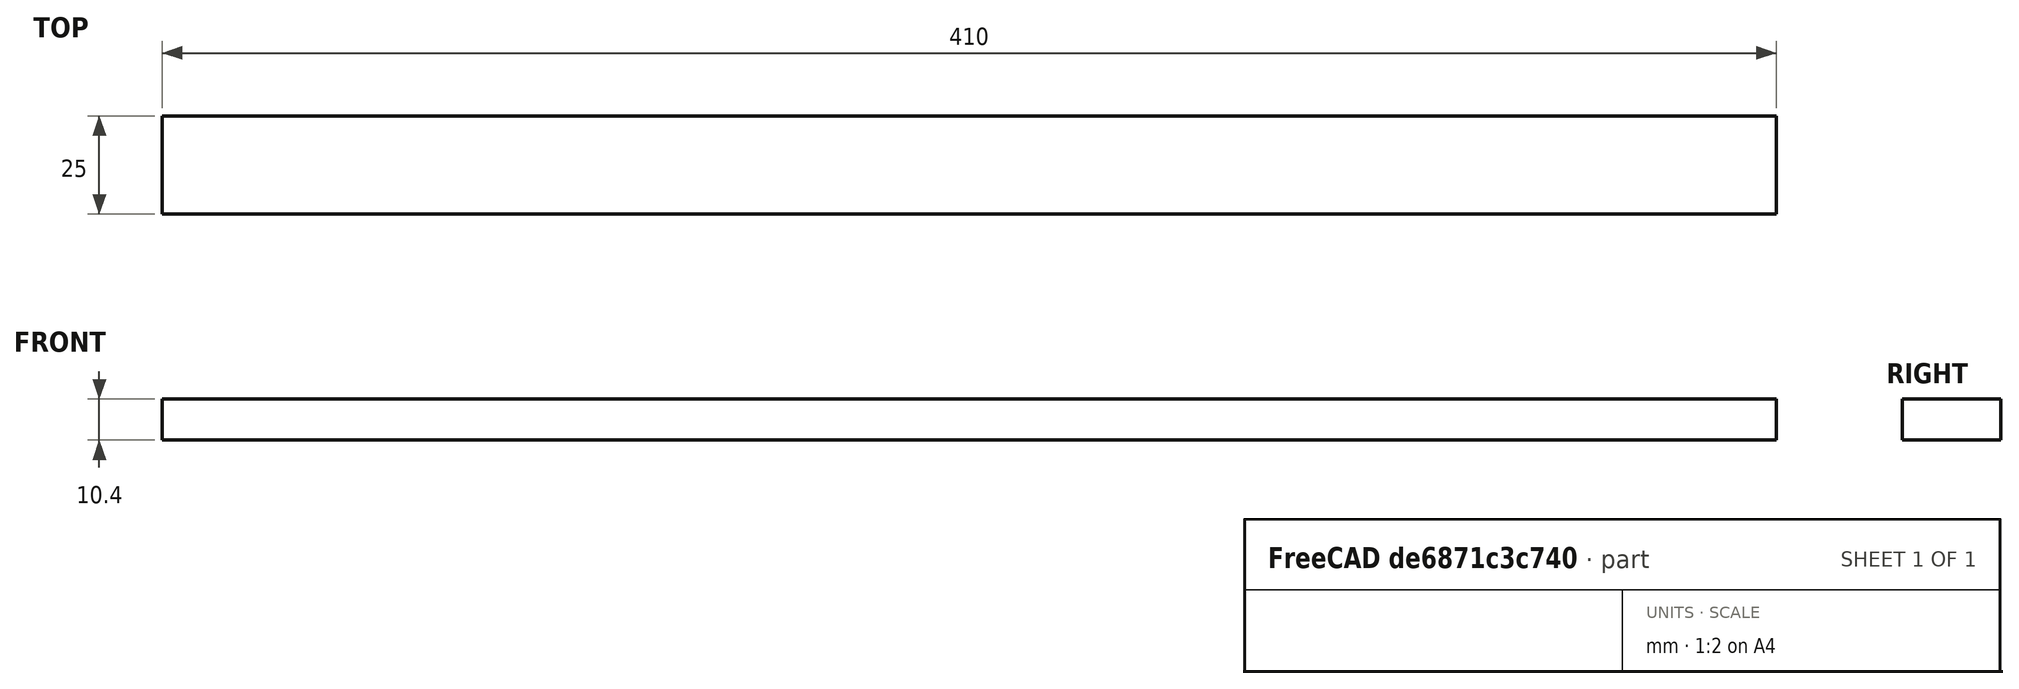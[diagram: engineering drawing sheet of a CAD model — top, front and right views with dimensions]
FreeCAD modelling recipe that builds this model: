
FCSTD DOCUMENT  (FreeCAD 0.19R24267 +99 (Git))
Label: Laufschinen
License: All rights reserved
LicenseURL: http://en.wikipedia.org/wiki/All_rights_reserved
objects: TechDraw::DrawProjGroupItem×3, TechDraw::DrawProjGroup×3, TechDraw::DrawViewDimension×3, Sketcher::SketchObject×1, PartDesign::Pad×1, PartDesign::Body×1, TechDraw::DrawSVGTemplate×1, TechDraw::DrawPage×1
note: 4 computed .brp shape members not serialized (recipe doc carries the construction recipe); baked Part::Feature solids carry a one-line shape summary decoded from their .brp

FEATURE [Sketcher::SketchObject] Sketch
  FullyConstrained = true
  MapMode = 5
  Support = -> [XY_Plane]
  sketch-geometry (4):
    g0: LineSegment StartX=-205 StartY=12.5 StartZ=0 EndX=205 EndY=12.5 EndZ=0
    g1: LineSegment StartX=205 StartY=12.5 StartZ=0 EndX=205 EndY=-12.5 EndZ=0
    g2: LineSegment StartX=205 StartY=-12.5 StartZ=0 EndX=-205 EndY=-12.5 EndZ=0
    g3: LineSegment StartX=-205 StartY=-12.5 StartZ=0 EndX=-205 EndY=12.5 EndZ=0
  constraints (11):
    c: Coincident(g0,g1)
    c: Coincident(g1,g2)
    c: Coincident(g2,g3)
    c: Coincident(g3,g0)
    c: Horizontal(g0)
    c: Horizontal(g2)
    c: Vertical(g1)
    c: Vertical(g3)
    c: DistanceX(g0,g0) = 410
    c: Symmetric(g0,g1,g-1)
    c: DistanceY(g1,g1) = 25
FEATURE [PartDesign::Pad] Pad
  Direction = (1,1,1)
  Length = 10.4
  Length2 = 100
  Profile = -> Sketch
  Type = 0
FEATURE [PartDesign::Body] Body
  Group = -> [Sketch,Pad]
  Origin = -> Origin
  Tip = -> Pad
FEATURE [TechDraw::DrawSVGTemplate] Template
  EditableTexts = APPROVER_NAME=APPROVER NAME; AUTHOR_NAME=AUTHOR NAME; DATE=YYYY-MM-DD; DN=DN; DOCUMENT_TYPE=Mechanical assembly drawing; OWNER_NAME=OWNER NAME; PM=PM; PN=PN; REVISION=REV A; RIGHTS=(R) DO NOT DUPLICATE THIS DRAWING TO THIRD PARTIES WITHOUT OWNER'S PERMISSION !; SCALE=M x:x; SHEET=99 of 99; SIZE=A4; TITLELINE-1=FreeCAD; TOLERANCE=+/- ?
  Height = 210
  Orientation = 1
  Width = 297
FEATURE [TechDraw::DrawProjGroupItem] ProjItem  label="Front"
  Caption = Seitenansicht (1:2)
  CoarseView = false
  Direction = (0,-1,0)
  Focus = 100
  HardHidden = false
  IsoCount = 0
  IsoHidden = false
  IsoVisible = false
  LockPosition = true
  Perspective = false
  Rotation = 0
  RotationVector = (1,0,0)
  Scale = 0.5
  ScaleType = 2
  SeamHidden = false
  SeamVisible = true
  SmoothHidden = false
  SmoothVisible = true
  Source = -> [Body]
  Type = 0
  X = 0
  XDirection = (1,0,0)
  Y = 0
FEATURE [TechDraw::DrawProjGroup] ProjGroup
  Anchor = -> ProjItem
  AutoDistribute = true
  LockPosition = false
  ProjectionType = 0
  Rotation = 0
  Scale = 0.5
  ScaleType = 2
  Source = -> [Body]
  Views = -> [ProjItem]
  X = 115.539
  Y = 184.854
  spacingX = 15
  spacingY = 15
FEATURE [TechDraw::DrawProjGroupItem] ProjItem001  label="Front001"
  Caption = Draufsicht (1:1)
  CoarseView = false
  Direction = (1,0,0)
  Focus = 100
  HardHidden = false
  IsoCount = 0
  IsoHidden = false
  IsoVisible = false
  LockPosition = true
  Perspective = false
  Rotation = 0
  RotationVector = (0,1,0)
  ScaleType = 2
  SeamHidden = false
  SeamVisible = true
  SmoothHidden = false
  SmoothVisible = true
  Source = -> [Body]
  Type = 0
  X = 0
  XDirection = (0,1,0)
  Y = 0
FEATURE [TechDraw::DrawProjGroup] ProjGroup001
  Anchor = -> ProjItem001
  AutoDistribute = true
  LockPosition = false
  ProjectionType = 0
  Rotation = 0
  ScaleType = 0
  Source = -> [Body]
  Views = -> [ProjItem001]
  X = 148.5
  Y = 105
  spacingX = 15
  spacingY = 15
FEATURE [TechDraw::DrawProjGroupItem] ProjItem002  label="Front002"
  Caption = Frontansicht (1:3)
  CoarseView = false
  Direction = (0,0,1)
  Focus = 100
  HardHidden = false
  IsoCount = 0
  IsoHidden = false
  IsoVisible = false
  LockPosition = true
  Perspective = false
  Rotation = 0
  RotationVector = (0,1,0)
  Scale = 0.333333
  ScaleType = 2
  SeamHidden = false
  SeamVisible = true
  SmoothHidden = false
  SmoothVisible = true
  Source = -> [Body]
  Type = 0
  X = 0
  XDirection = (0,1,0)
  Y = 0
FEATURE [TechDraw::DrawProjGroup] ProjGroup002
  Anchor = -> ProjItem002
  AutoDistribute = true
  LockPosition = false
  ProjectionType = 0
  Rotation = 0
  Scale = 0.333333
  ScaleType = 2
  Source = -> [Body]
  Views = -> [ProjItem002]
  X = 28.8883
  Y = 99.2233
  spacingX = 15
  spacingY = 15
FEATURE [TechDraw::DrawViewDimension] Dimension
  Arbitrary = false
  ArbitraryTolerances = false
  EqualTolerance = true
  FormatSpec = %.2f
  FormatSpecOverTolerance = %+.2f
  FormatSpecUnderTolerance = %+.2f
  Inverted = false
  LockPosition = false
  MeasureType = 1
  OverTolerance = 0
  References2D = -> [ProjItem]
  Rotation = 0
  ScaleType = 0
  TheoreticalExact = false
  Type = 1
  UnderTolerance = 0
  X = 0
  Y = -2.6
FEATURE [TechDraw::DrawViewDimension] Dimension001
  Arbitrary = false
  ArbitraryTolerances = false
  EqualTolerance = true
  FormatSpec = %.2f
  FormatSpecOverTolerance = %+.2f
  FormatSpecUnderTolerance = %+.2f
  Inverted = false
  LockPosition = false
  MeasureType = 1
  OverTolerance = 0
  References2D = -> [ProjItem]
  Rotation = 0
  ScaleType = 0
  TheoreticalExact = false
  Type = 2
  UnderTolerance = 0
  X = -109.296
  Y = 1.01942
FEATURE [TechDraw::DrawViewDimension] Dimension002
  Arbitrary = false
  ArbitraryTolerances = false
  EqualTolerance = true
  FormatSpec = %.2f
  FormatSpecOverTolerance = %+.2f
  FormatSpecUnderTolerance = %+.2f
  Inverted = false
  LockPosition = false
  MeasureType = 1
  OverTolerance = 0
  References2D = -> [ProjItem001]
  Rotation = 0
  ScaleType = 0
  TheoreticalExact = false
  Type = 1
  UnderTolerance = 0
  X = 0
  Y = -5.2
FEATURE [TechDraw::DrawPage] Page
  KeepUpdated = true
  NextBalloonIndex = 1
  ProjectionType = 0
  Template = -> Template
  Views = -> [ProjGroup,ProjGroup001,ProjGroup002,Dimension,Dimension001,Dimension002]
